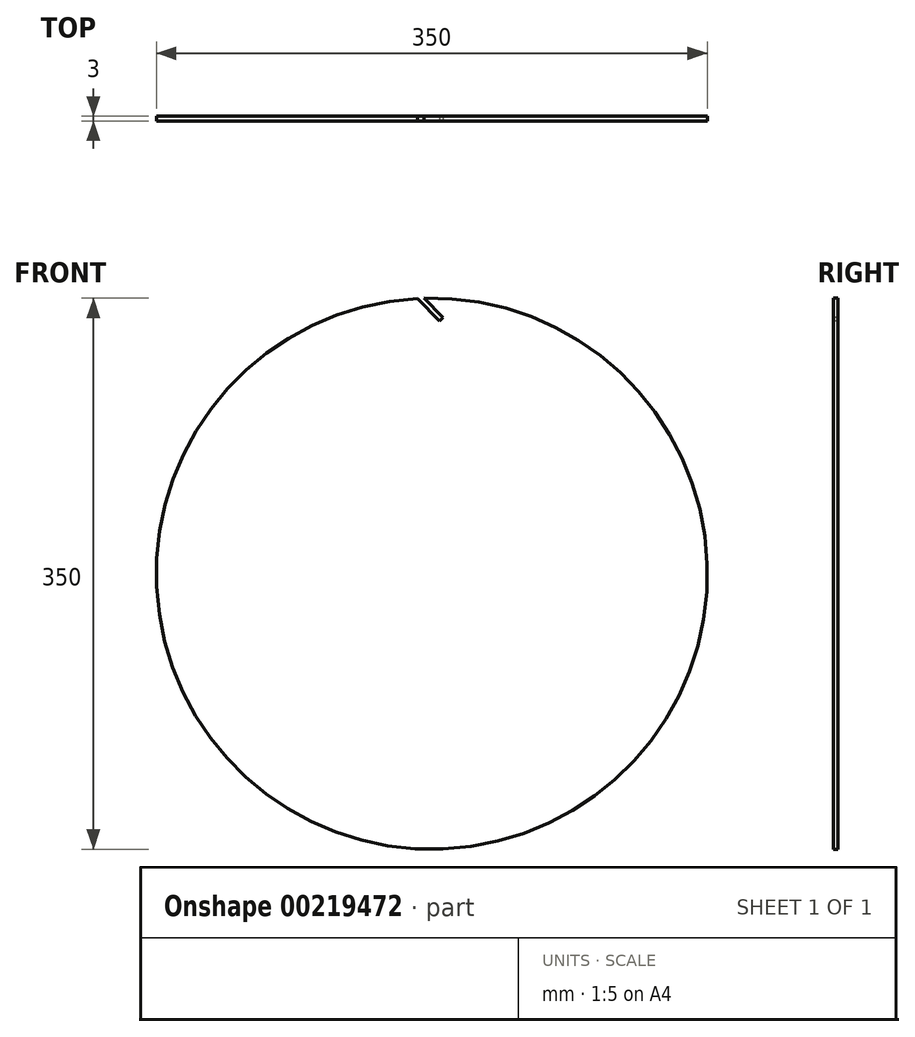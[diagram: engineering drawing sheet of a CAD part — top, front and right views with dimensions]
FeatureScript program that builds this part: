
annotation { "Feature Type Name" : "Feature", "Feature Type Description" : "" }
export const myFeature = defineFeature(function(context is Context, id is Id, definition is map)
    precondition{}
    {
        {
            var Q0;
            Q0=qCreatedBy(makeId("Front.planeOp"),FACE);
            var sketch = newSketch(context, id + "F0", { "sketchPlane" : qUnion([Q0])});
            skCircle(sketch, "E0", {"center": v(0, 0) * mm, "radius": 175 * mm});
            skSolve(sketch);
        }
        {
            var Q0;
            Q0=makeQuery(id+"F0.imprint","IMPRINT",FACE,{"disambiguationData":[TD([[makeQuery(id+"F0.imprint","IMPRINT",EDGE,{"derivedFrom":sQuery(id+"F0.wireOp",EDGE,"E0")}),1.0]])]});
            extrude(context, id + "F1", {"entities" : qUnion([Q0]), "oppositeDirection" : true, "depth" : 3 * mm});
        }
        {
            var Q0;
            Q0=makeQuery(id+"F0.imprint","IMPRINT",FACE,{"disambiguationData":[TD([[makeQuery(id+"F0.imprint","IMPRINT",EDGE,{"derivedFrom":sQuery(id+"F0.wireOp",EDGE,"E0")}),1.0]])]});
            var sketch = newSketch(context, id + "F2", { "sketchPlane" : qUnion([Q0])});
            skLineSegment(sketch, "E1", {"start": v(-9.2, 174.76) * mm, "end": v(4.95, 160.62) * mm});
            skLineSegment(sketch, "E2", {"start": v(7.07, 162.74) * mm, "end": v(4.95, 160.62) * mm});
            skLineSegment(sketch, "E3", {"start": v(7.07, 162.74) * mm, "end": v(-7.07, 176.88) * mm});
            skLineSegment(sketch, "E4", {"start": v(-9.2, 174.76) * mm, "end": v(-7.07, 176.88) * mm});
            skLineSegment(sketch, "E5", {"start": v(0, 169.8) * mm, "end": v(-2.12, 167.69) * mm, "construction": true});
            skSolve(sketch);
        }
        {
            var Q0;
            {var subQ0=sQuery(id+"F2.wireOp",EDGE,"E1");Q0=makeQuery(id+"F2.imprint","IMPRINT",FACE,{"disambiguationData":[TD([[makeQuery(id+"F2.imprint","IMPRINT",EDGE,{"derivedFrom":subQ0}),1.0]])]});}
            extrude(context, id + "F3", {"entities" : qUnion([Q0]), "operationType" : NewBodyOperationType.REMOVE, "endBound" : BoundingType.THROUGH_ALL, "oppositeDirection" : true, "depth" : 25 * mm});
        }
        {
            var Q0;
            Q0=qCreatedBy(makeId("Top.planeOp"),FACE);
            var sketch = newSketch(context, id + "F4", { "sketchPlane" : qUnion([Q0])});
            skLineSegment(sketch, "E6", {"start": v(0, 76.69) * mm, "end": v(0, -73.16) * mm});
            skSolve(sketch);
        }
    });
